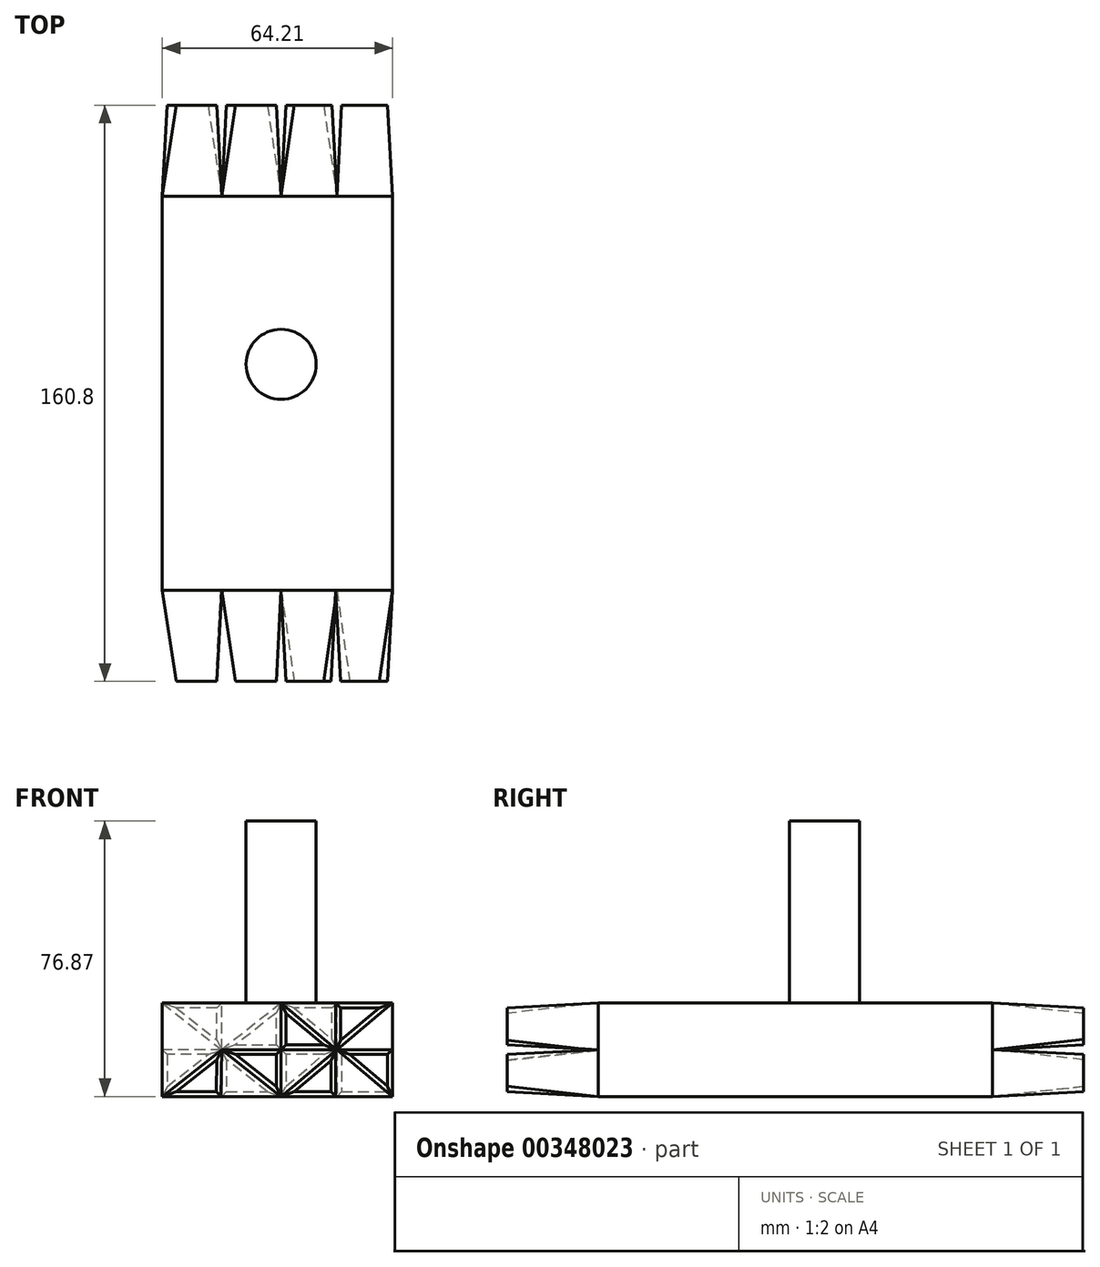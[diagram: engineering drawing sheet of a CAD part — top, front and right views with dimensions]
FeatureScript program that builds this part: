
annotation { "Feature Type Name" : "Feature", "Feature Type Description" : "" }
export const myFeature = defineFeature(function(context is Context, id is Id, definition is map)
    precondition{}
    {
        {
            var Q0;
            Q0=qCreatedBy(makeId("Front.planeOp"),FACE);
            var sketch = newSketch(context, id + "F0", { "sketchPlane" : qUnion([Q0])});
            skLineSegment(sketch, "E0.bottom", {"start": v(-33.14, -26.07) * mm, "end": v(31.07, -26.07) * mm});
            skLineSegment(sketch, "E0.top", {"start": v(-33.14, 0) * mm, "end": v(31.07, 0) * mm});
            skLineSegment(sketch, "E0.left", {"start": v(-33.14, -26.07) * mm, "end": v(-33.14, 0) * mm});
            skLineSegment(sketch, "E0.right", {"start": v(31.07, -26.07) * mm, "end": v(31.07, 0) * mm});
            skSolve(sketch);
        }
        {
            var Q0;
            Q0=makeQuery(id+"F0.imprint","IMPRINT",FACE,{"disambiguationData":[TD([[makeQuery(id+"F0.imprint","IMPRINT",EDGE,{"derivedFrom":sQuery(id+"F0.wireOp",EDGE,"E0.bottom")}),1.0]])]});
            extrude(context, id + "F1", {"entities" : qUnion([Q0]), "depth" : 110 * mm});
        }
        {
            var Q0;
            Q0=makeQuery(id+"F1.opExtrude","CAP_FACE",FACE,{"disambiguationData":[OSD([sQuery(id+"F0.wireOp",EDGE,"E0.bottom"),sQuery(id+"F0.wireOp",EDGE,"E0.top"),sQuery(id+"F0.wireOp",EDGE,"E0.left"),sQuery(id+"F0.wireOp",EDGE,"E0.right")])],"isStart":true});
            var sketch = newSketch(context, id + "F2", { "sketchPlane" : qUnion([Q0])});
            skLineSegment(sketch, "E1", {"start": v(0, 0) * mm, "end": v(0, -26.07) * mm});
            skLineSegment(sketch, "E2", {"start": v(0, -26.07) * mm, "end": v(33.14, 0) * mm});
            skLineSegment(sketch, "E3", {"start": v(33.14, 0) * mm, "end": v(0, -26.07) * mm});
            skLineSegment(sketch, "E4", {"start": v(-31.07, 0) * mm, "end": v(0, -26.07) * mm});
            skLineSegment(sketch, "E5", {"start": v(-31.07, -26.07) * mm, "end": v(0, 0) * mm});
            skLineSegment(sketch, "E6", {"start": v(0, 0) * mm, "end": v(33.14, -26.07) * mm});
            skLineSegment(sketch, "E7", {"start": v(33.14, -26.07) * mm, "end": v(-31.07, -26.07) * mm});
            skLineSegment(sketch, "E8", {"start": v(33.14, -13.03) * mm, "end": v(-31.07, -13.03) * mm});
            skLineSegment(sketch, "E9", {"start": v(-31.07, -13.03) * mm, "end": v(-31.07, 0) * mm});
            skLineSegment(sketch, "E10", {"start": v(-31.07, 0) * mm, "end": v(33.14, 0) * mm});
            skLineSegment(sketch, "E11", {"start": v(33.14, 0) * mm, "end": v(33.14, -26.07) * mm});
            skLineSegment(sketch, "E12", {"start": v(-31.07, -26.07) * mm, "end": v(-31.07, 0) * mm});
            skLineSegment(sketch, "E13", {"start": v(-15.53, 0) * mm, "end": v(-15.53, -26.07) * mm});
            skPoint(sketch, "E13.startSnap0", {"position": v(-15.53, -13.03) * mm});
            skLineSegment(sketch, "E14", {"start": v(16.57, 0) * mm, "end": v(16.57, -26.07) * mm});
            skPoint(sketch, "E14.startSnap0", {"position": v(16.57, -13.03) * mm});
            skSolve(sketch);
        }
        {
            var Q0;
            {var subQ0=sQuery(id+"F2.wireOp",EDGE,"E11");var subQ3=sQuery(id+"F2.wireOp",EDGE,"E8");var subQ5=makeQuery(id+"F2.imprint","INTERSECT",VERTEX,{"derivedFrom":[subQ3,subQ0]});Q0=makeQuery(id+"F2.imprint","IMPRINT",FACE,{"disambiguationData":[TD([[makeQuery(id+"F2.imprint","IMPRINT",EDGE,{"disambiguationData":[TD([[subQ5,1.0]])],"derivedFrom":subQ0}),1.0]])]});}
            var Q1;
            {var subQ0=sQuery(id+"F2.wireOp",EDGE,"E10");var subQ3=sQuery(id+"F2.wireOp",EDGE,"E13");var subQ5=makeQuery(id+"F2.imprint","INTERSECT",VERTEX,{"derivedFrom":[subQ0,subQ3]});Q1=makeQuery(id+"F2.imprint","IMPRINT",FACE,{"disambiguationData":[TD([[makeQuery(id+"F2.imprint","IMPRINT",EDGE,{"disambiguationData":[TD([[subQ5,1.0]])],"derivedFrom":subQ0}),1.0]])]});}
            var Q2;
            {var subQ0=sQuery(id+"F2.wireOp",EDGE,"E12");var subQ3=sQuery(id+"F2.wireOp",EDGE,"E8");var subQ5=makeQuery(id+"F2.imprint","INTERSECT",VERTEX,{"derivedFrom":[subQ3,subQ0]});Q2=makeQuery(id+"F2.imprint","IMPRINT",FACE,{"disambiguationData":[TD([[makeQuery(id+"F2.imprint","IMPRINT",EDGE,{"disambiguationData":[TD([[subQ5,-1.0]])],"derivedFrom":subQ0}),-1.0]])]});}
            var Q3;
            {var subQ1=sQuery(id+"F2.wireOp",EDGE,"E1");var subQ3=sQuery(id+"F2.wireOp",EDGE,"E8");var subQ4=makeQuery(id+"F2.imprint","INTERSECT",VERTEX,{"derivedFrom":[subQ1,subQ3]});Q3=makeQuery(id+"F2.imprint","IMPRINT",FACE,{"disambiguationData":[TD([[makeQuery(id+"F2.imprint","IMPRINT",EDGE,{"disambiguationData":[TD([[subQ4,1.0]])],"derivedFrom":subQ1}),1.0]])]});}
            var Q4;
            {var subQ0=sQuery(id+"F2.wireOp",EDGE,"E7");var subQ3=sQuery(id+"F2.wireOp",EDGE,"E14");var subQ5=makeQuery(id+"F2.imprint","INTERSECT",VERTEX,{"derivedFrom":[subQ0,subQ3]});Q4=makeQuery(id+"F2.imprint","IMPRINT",FACE,{"disambiguationData":[TD([[makeQuery(id+"F2.imprint","IMPRINT",EDGE,{"disambiguationData":[TD([[subQ5,-1.0]])],"derivedFrom":subQ0}),-1.0]])]});}
            var Q5;
            {var subQ0=sQuery(id+"F2.wireOp",EDGE,"E10");var subQ3=sQuery(id+"F2.wireOp",EDGE,"E14");var subQ5=makeQuery(id+"F2.imprint","INTERSECT",VERTEX,{"derivedFrom":[subQ0,subQ3]});Q5=makeQuery(id+"F2.imprint","IMPRINT",FACE,{"disambiguationData":[TD([[makeQuery(id+"F2.imprint","IMPRINT",EDGE,{"disambiguationData":[TD([[subQ5,1.0]])],"derivedFrom":subQ0}),1.0]])]});}
            var Q6;
            {var subQ0=sQuery(id+"F2.wireOp",EDGE,"E7");var subQ3=sQuery(id+"F2.wireOp",EDGE,"E13");var subQ5=makeQuery(id+"F2.imprint","INTERSECT",VERTEX,{"derivedFrom":[subQ0,subQ3]});Q6=makeQuery(id+"F2.imprint","IMPRINT",FACE,{"disambiguationData":[TD([[makeQuery(id+"F2.imprint","IMPRINT",EDGE,{"disambiguationData":[TD([[subQ5,-1.0]])],"derivedFrom":subQ0}),-1.0]])]});}
            var Q7;
            {var subQ1=sQuery(id+"F2.wireOp",EDGE,"E1");var subQ3=sQuery(id+"F2.wireOp",EDGE,"E8");var subQ4=makeQuery(id+"F2.imprint","INTERSECT",VERTEX,{"derivedFrom":[subQ1,subQ3]});Q7=makeQuery(id+"F2.imprint","IMPRINT",FACE,{"disambiguationData":[TD([[makeQuery(id+"F2.imprint","IMPRINT",EDGE,{"disambiguationData":[TD([[subQ4,-1.0]])],"derivedFrom":subQ1}),-1.0]])]});}
            extrude(context, id + "F3", {"entities" : qUnion([Q0, Q1, Q2, Q3, Q4, Q5, Q6, Q7]), "operationType" : NewBodyOperationType.ADD, "depth" : 25.4 * mm, "hasDraft" : true, "draftAngle" : 3 * degree, "draftPullDirection" : true});
        }
        {
            var Q0;
            Q0=makeQuery(id+"F1.opExtrude","CAP_FACE",FACE,{"disambiguationData":[OSD([sQuery(id+"F0.wireOp",EDGE,"E0.bottom"),sQuery(id+"F0.wireOp",EDGE,"E0.top"),sQuery(id+"F0.wireOp",EDGE,"E0.left"),sQuery(id+"F0.wireOp",EDGE,"E0.right")])],"isStart":false});
            var sketch = newSketch(context, id + "F4", { "sketchPlane" : qUnion([Q0])});
            skLineSegment(sketch, "E15", {"start": v(0, -26.07) * mm, "end": v(0, 0) * mm});
            skLineSegment(sketch, "E16", {"start": v(0, 0) * mm, "end": v(-33.14, -26.07) * mm});
            skLineSegment(sketch, "E17", {"start": v(-33.14, -26.07) * mm, "end": v(31.07, -26.07) * mm});
            skLineSegment(sketch, "E18", {"start": v(31.07, -26.07) * mm, "end": v(0, 0) * mm});
            skLineSegment(sketch, "E19", {"start": v(31.07, 0) * mm, "end": v(-33.14, 0) * mm});
            skLineSegment(sketch, "E20", {"start": v(-33.14, 0) * mm, "end": v(-33.14, -26.07) * mm});
            skLineSegment(sketch, "E21", {"start": v(31.07, 0) * mm, "end": v(31.07, -26.07) * mm});
            skLineSegment(sketch, "E22", {"start": v(0, -26.07) * mm, "end": v(31.07, 0) * mm});
            skLineSegment(sketch, "E23", {"start": v(-33.14, 0) * mm, "end": v(0, -26.07) * mm});
            skLineSegment(sketch, "E24", {"start": v(31.07, -13.03) * mm, "end": v(-33.14, -13.03) * mm});
            skLineSegment(sketch, "E25", {"start": v(-33.14, -13.03) * mm, "end": v(-16.57, -13.03) * mm});
            skLineSegment(sketch, "E26", {"start": v(-16.57, -13.03) * mm, "end": v(-16.57, 0) * mm});
            skLineSegment(sketch, "E27", {"start": v(-16.57, 0) * mm, "end": v(-16.57, -13.03) * mm});
            skLineSegment(sketch, "E28", {"start": v(-16.84, -26.07) * mm, "end": v(-16.57, -13.03) * mm});
            skLineSegment(sketch, "E29", {"start": v(15.24, -26.07) * mm, "end": v(15.24, 0) * mm});
            skSolve(sketch);
        }
        {
            var Q0;
            Q0=qCreatedBy(makeId("Front.planeOp"),FACE);
            cPlane(context, id + "F5", {"entities" : qUnion([Q0]), "cplaneType" : CPlaneType.OFFSET, "offset" : 76.2 * mm, "width" : 152.4 * mm, "height" : 152.4 * mm});
        }
        {
            var Q0;
            {var subQ1=sQuery(id+"F4.wireOp",EDGE,"E17");var subQ3=sQuery(id+"F4.wireOp",EDGE,"E29");var subQ4=makeQuery(id+"F4.imprint","INTERSECT",VERTEX,{"derivedFrom":[subQ1,subQ3]});Q0=makeQuery(id+"F4.imprint","IMPRINT",FACE,{"disambiguationData":[TD([[makeQuery(id+"F4.imprint","IMPRINT",EDGE,{"disambiguationData":[TD([[subQ4,-1.0]])],"derivedFrom":subQ3}),1.0]])]});}
            var Q1;
            {var subQ0=sQuery(id+"F4.wireOp",EDGE,"E21");var subQ3=sQuery(id+"F4.wireOp",EDGE,"E24");var subQ5=makeQuery(id+"F4.imprint","INTERSECT",VERTEX,{"derivedFrom":[subQ0,subQ3]});Q1=makeQuery(id+"F4.imprint","IMPRINT",FACE,{"disambiguationData":[TD([[makeQuery(id+"F4.imprint","IMPRINT",EDGE,{"disambiguationData":[TD([[subQ5,1.0]])],"derivedFrom":subQ0}),1.0]])]});}
            var Q2;
            {var subQ1=sQuery(id+"F4.wireOp",EDGE,"E15");var subQ3=sQuery(id+"F4.wireOp",EDGE,"E24");var subQ4=makeQuery(id+"F4.imprint","INTERSECT",VERTEX,{"derivedFrom":[subQ1,subQ3]});Q2=makeQuery(id+"F4.imprint","IMPRINT",FACE,{"disambiguationData":[TD([[makeQuery(id+"F4.imprint","IMPRINT",EDGE,{"disambiguationData":[TD([[subQ4,1.0]])],"derivedFrom":subQ1}),1.0]])]});}
            var Q3;
            {var subQ3=sQuery(id+"F4.wireOp",EDGE,"E28");Q3=makeQuery(id+"F4.imprint","IMPRINT",FACE,{"disambiguationData":[TD([[makeQuery(id+"F4.imprint","IMPRINT",EDGE,{"derivedFrom":subQ3}),1.0]])]});}
            var Q4;
            {var subQ3=sQuery(id+"F4.wireOp",EDGE,"E25");Q4=makeQuery(id+"F4.imprint","IMPRINT",FACE,{"disambiguationData":[TD([[makeQuery(id+"F4.imprint","IMPRINT",EDGE,{"derivedFrom":subQ3}),1.0]])]});}
            var Q5;
            {var subQ0=sQuery(id+"F4.wireOp",EDGE,"E29");var subQ5=sQuery(id+"F4.wireOp",EDGE,"E19");var subQ7=makeQuery(id+"F4.imprint","INTERSECT",VERTEX,{"derivedFrom":[subQ5,subQ0]});Q5=makeQuery(id+"F4.imprint","IMPRINT",FACE,{"disambiguationData":[TD([[makeQuery(id+"F4.imprint","IMPRINT",EDGE,{"disambiguationData":[TD([[subQ7,1.0]])],"derivedFrom":subQ0}),-1.0]])]});}
            var Q6;
            {var subQ3=sQuery(id+"F4.wireOp",EDGE,"E27");Q6=makeQuery(id+"F4.imprint","IMPRINT",FACE,{"disambiguationData":[TD([[makeQuery(id+"F4.imprint","IMPRINT",EDGE,{"derivedFrom":subQ3}),1.0]])]});}
            var Q7;
            {var subQ1=sQuery(id+"F4.wireOp",EDGE,"E15");var subQ3=sQuery(id+"F4.wireOp",EDGE,"E24");var subQ4=makeQuery(id+"F4.imprint","INTERSECT",VERTEX,{"derivedFrom":[subQ1,subQ3]});Q7=makeQuery(id+"F4.imprint","IMPRINT",FACE,{"disambiguationData":[TD([[makeQuery(id+"F4.imprint","IMPRINT",EDGE,{"disambiguationData":[TD([[subQ4,1.0]])],"derivedFrom":subQ3}),-1.0]])]});}
            extrude(context, id + "F6", {"entities" : qUnion([Q0, Q1, Q2, Q3, Q4, Q5, Q6, Q7]), "operationType" : NewBodyOperationType.ADD, "depth" : 25.4 * mm, "hasDraft" : true, "draftAngle" : 3 * degree, "draftPullDirection" : true});
        }
        {
            var Q0;
            Q0=qCreatedBy(makeId("Top.planeOp"),FACE);
            var sketch = newSketch(context, id + "F7", { "sketchPlane" : qUnion([Q0])});
            skCircle(sketch, "E30", {"center": v(-0.87, -47.67) * mm, "radius": 32.2 * mm});
            skPoint(sketch, "E30.first.point", {"position": v(-32.86, -44.08) * mm});
            skPoint(sketch, "E30.second.point", {"position": v(31.3, -46.69) * mm});
            skPoint(sketch, "E30.third.point", {"position": v(0, -15.49) * mm});
            skSolve(sketch);
        }
        {
            var Q0;
            Q0=makeQuery(id+"F7.imprint","IMPRINT",FACE,{"disambiguationData":[TD([[makeQuery(id+"F7.imprint","IMPRINT",EDGE,{"derivedFrom":sQuery(id+"F7.wireOp",EDGE,"E30")}),1.0]])]});
            var sketch = newSketch(context, id + "F8", { "sketchPlane" : qUnion([Q0])});
            skCircle(sketch, "E31", {"center": v(0, -46.9) * mm, "radius": 9.78 * mm});
            skSolve(sketch);
        }
        {
            var Q0;
            Q0=makeQuery(id+"F8.imprint","IMPRINT",FACE,{"disambiguationData":[TD([[makeQuery(id+"F8.imprint","IMPRINT",EDGE,{"derivedFrom":sQuery(id+"F8.wireOp",EDGE,"E31")}),1.0]])]});
            var Q1;
            Q1=sQuery(id+"F8.wireOp",EDGE,"E31");
            extrude(context, id + "F9", {"entities" : qUnion([Q0]), "surfaceEntities" : qUnion([Q1]), "depth" : 50.8 * mm});
        }
        {
            var Q0;
            Q0=makeQuery(id+"F1.opExtrude","SWEPT_BODY",BODY,{"disambiguationData":[OSD([sQuery(id+"F0.wireOp",EDGE,"E0.bottom"),sQuery(id+"F0.wireOp",EDGE,"E0.top"),sQuery(id+"F0.wireOp",EDGE,"E0.left"),sQuery(id+"F0.wireOp",EDGE,"E0.right")])]});
            transform(context, id + "F10", {"entities" : qUnion([Q0]), "transformType" : TransformType.TRANSLATION_3D, "dx" : 0 * mm, "dy" : 0 * mm, "dz" : 0 * mm, "makeCopy" : true});
        }
    });
